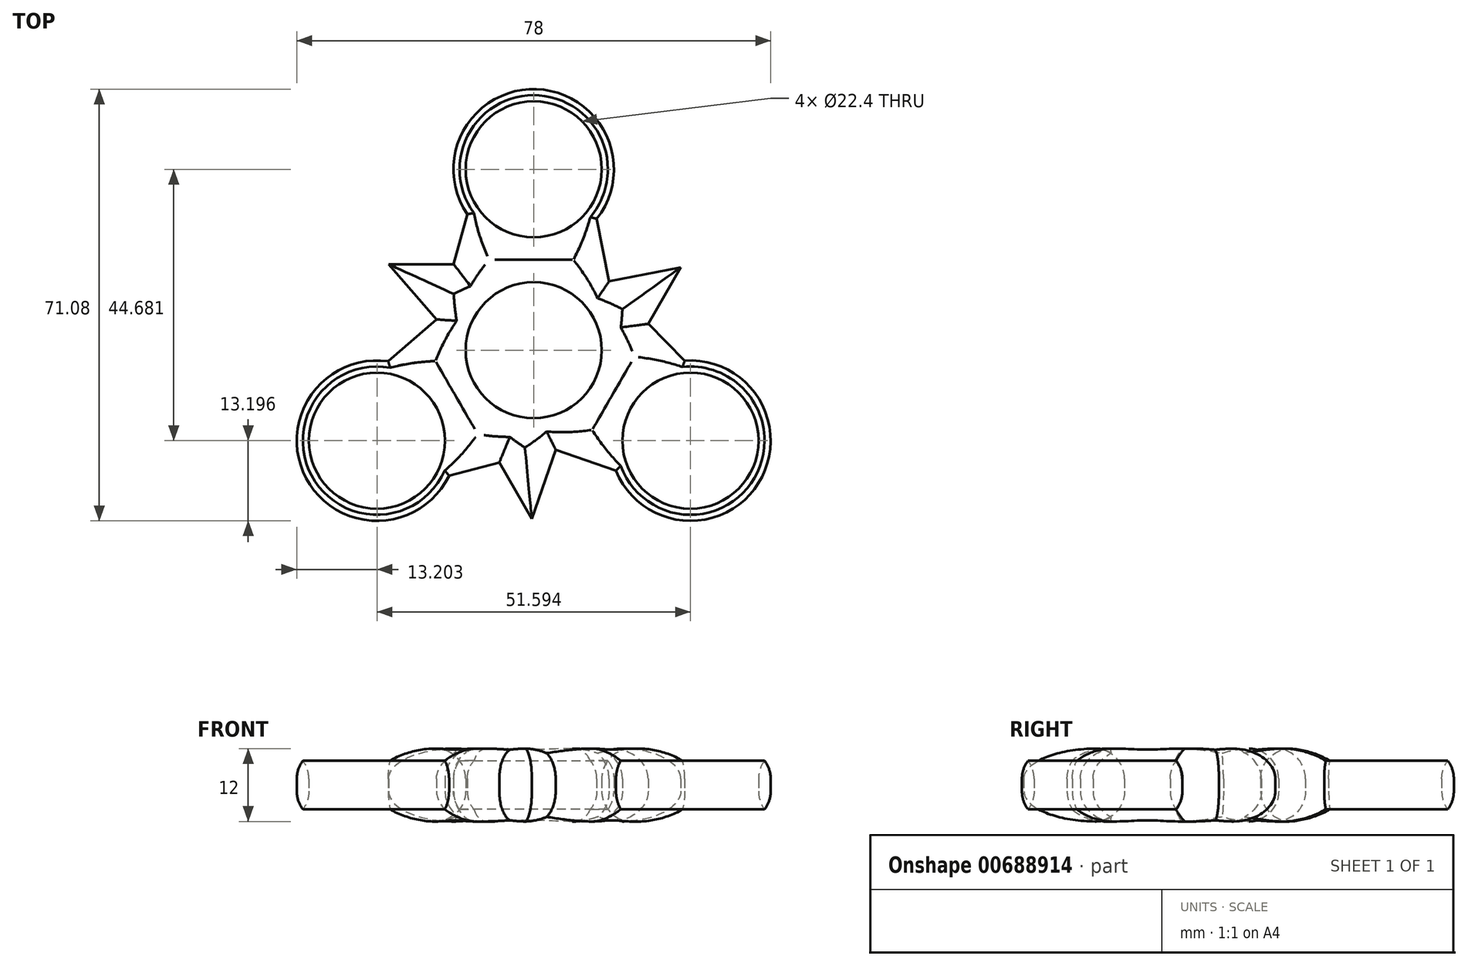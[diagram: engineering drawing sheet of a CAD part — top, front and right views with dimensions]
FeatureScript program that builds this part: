
annotation { "Feature Type Name" : "Feature", "Feature Type Description" : "" }
export const myFeature = defineFeature(function(context is Context, id is Id, definition is map)
    precondition{}
    {
        {
            var Q0;
            Q0=qCreatedBy(makeId("Top.planeOp"),FACE);
            var sketch = newSketch(context, id + "F0", { "sketchPlane" : qUnion([Q0])});
            skCircle(sketch, "E0", {"center": v(0, 0) * mm, "radius": 11.2 * mm});
            skCircle(sketch, "E1", {"center": v(0, 29.79) * mm, "radius": 11.2 * mm});
            skArc(sketch, "E2", {"start": v(10.39, 21.64) * mm, "mid": v(0.46, 42.98) * mm, "end": v(-10.93, 22.4) * mm});
            skArc(sketch, "E3.1.0", {"start": v(-23.94, -1.83) * mm, "mid": v(-37.45, -21.09) * mm, "end": v(-13.93, -20.66) * mm});
            skCircle(sketch, "E3.1.1", {"center": v(-25.8, -14.9) * mm, "radius": 11.2 * mm});
            skArc(sketch, "E3.2.0", {"start": v(13.55, -19.82) * mm, "mid": v(37, -21.9) * mm, "end": v(24.86, -1.73) * mm});
            skCircle(sketch, "E3.2.1", {"center": v(25.8, -14.9) * mm, "radius": 11.2 * mm});
            skLineSegment(sketch, "E4", {"start": v(-10.93, 22.4) * mm, "end": v(-13.17, 14.15) * mm});
            skLineSegment(sketch, "E5", {"start": v(-13.17, 14.15) * mm, "end": v(-23.9, 14.15) * mm});
            skLineSegment(sketch, "E6", {"start": v(-23.9, 14.15) * mm, "end": v(-16, 5.07) * mm});
            skLineSegment(sketch, "E7", {"start": v(-16, 5.07) * mm, "end": v(-23.94, -1.83) * mm});
            skLineSegment(sketch, "E8.1.0", {"start": v(-13.93, -20.66) * mm, "end": v(-5.67, -18.49) * mm});
            skLineSegment(sketch, "E8.1.1", {"start": v(-5.67, -18.49) * mm, "end": v(-0.3, -27.77) * mm});
            skLineSegment(sketch, "E8.1.2", {"start": v(-0.3, -27.77) * mm, "end": v(3.61, -16.4) * mm});
            skLineSegment(sketch, "E8.1.3", {"start": v(3.61, -16.4) * mm, "end": v(13.55, -19.82) * mm});
            skLineSegment(sketch, "E8.2.0", {"start": v(24.86, -1.73) * mm, "end": v(18.84, 4.33) * mm});
            skLineSegment(sketch, "E8.2.1", {"start": v(18.84, 4.33) * mm, "end": v(24.2, 13.62) * mm});
            skLineSegment(sketch, "E8.2.2", {"start": v(24.2, 13.62) * mm, "end": v(12.4, 11.32) * mm});
            skLineSegment(sketch, "E8.2.3", {"start": v(12.4, 11.32) * mm, "end": v(10.39, 21.64) * mm});
            skSolve(sketch);
        }
        {
            var Q0;
            Q0 = qSketchRegion(id + "F0", true);
            extrude(context, id + "F1", {"entities" : qUnion([Q0]), "depth" : 12 * mm, "offsetDistance" : 25 * mm});
        }
        {
            var Q0;
            Q0=makeQuery(id+"F1.opExtrude","CAP_FACE",FACE,{"disambiguationData":[OSD([sQuery(id+"F0.wireOp",EDGE,"E0"),sQuery(id+"F0.wireOp",EDGE,"E1"),sQuery(id+"F0.wireOp",EDGE,"E2"),sQuery(id+"F0.wireOp",EDGE,"E3.1.0"),sQuery(id+"F0.wireOp",EDGE,"E3.1.1"),sQuery(id+"F0.wireOp",EDGE,"E3.2.0"),sQuery(id+"F0.wireOp",EDGE,"E3.2.1"),sQuery(id+"F0.wireOp",EDGE,"E4"),sQuery(id+"F0.wireOp",EDGE,"E5"),sQuery(id+"F0.wireOp",EDGE,"E6"),sQuery(id+"F0.wireOp",EDGE,"E7"),sQuery(id+"F0.wireOp",EDGE,"E8.1.0"),sQuery(id+"F0.wireOp",EDGE,"E8.1.1"),sQuery(id+"F0.wireOp",EDGE,"E8.1.2"),sQuery(id+"F0.wireOp",EDGE,"E8.1.3"),sQuery(id+"F0.wireOp",EDGE,"E8.2.0"),sQuery(id+"F0.wireOp",EDGE,"E8.2.1"),sQuery(id+"F0.wireOp",EDGE,"E8.2.2"),sQuery(id+"F0.wireOp",EDGE,"E8.2.3")])],"isStart":false});
            var Q1;
            Q1=makeQuery(id+"F1.opExtrude","CAP_FACE",FACE,{"disambiguationData":[OSD([sQuery(id+"F0.wireOp",EDGE,"E0"),sQuery(id+"F0.wireOp",EDGE,"E1"),sQuery(id+"F0.wireOp",EDGE,"E2"),sQuery(id+"F0.wireOp",EDGE,"E3.1.0"),sQuery(id+"F0.wireOp",EDGE,"E3.1.1"),sQuery(id+"F0.wireOp",EDGE,"E3.2.0"),sQuery(id+"F0.wireOp",EDGE,"E3.2.1"),sQuery(id+"F0.wireOp",EDGE,"E4"),sQuery(id+"F0.wireOp",EDGE,"E5"),sQuery(id+"F0.wireOp",EDGE,"E6"),sQuery(id+"F0.wireOp",EDGE,"E7"),sQuery(id+"F0.wireOp",EDGE,"E8.1.0"),sQuery(id+"F0.wireOp",EDGE,"E8.1.1"),sQuery(id+"F0.wireOp",EDGE,"E8.1.2"),sQuery(id+"F0.wireOp",EDGE,"E8.1.3"),sQuery(id+"F0.wireOp",EDGE,"E8.2.0"),sQuery(id+"F0.wireOp",EDGE,"E8.2.1"),sQuery(id+"F0.wireOp",EDGE,"E8.2.2"),sQuery(id+"F0.wireOp",EDGE,"E8.2.3")])],"isStart":true});
            fillet(context, id + "F2", {"entities" : qUnion([Q0, Q1]), "radius" : 5 * mm, "tangentPropagation" : true, "allowEdgeOverflow" : false});
        }
    });
